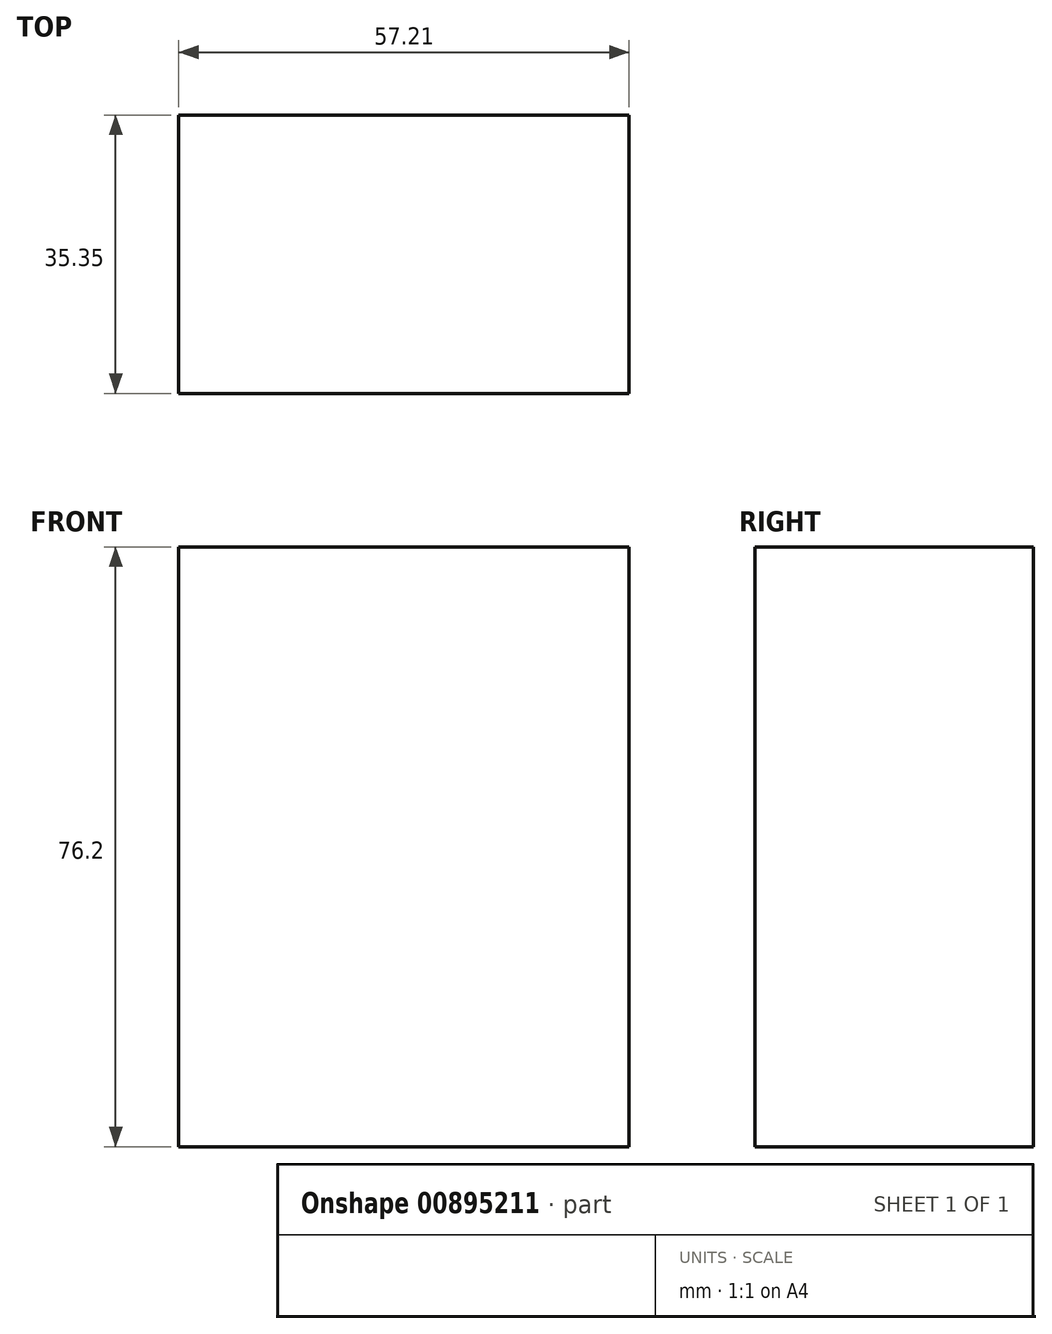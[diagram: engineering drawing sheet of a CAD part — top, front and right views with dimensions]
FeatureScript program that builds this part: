
annotation { "Feature Type Name" : "Feature", "Feature Type Description" : "" }
export const myFeature = defineFeature(function(context is Context, id is Id, definition is map)
    precondition{}
    {
        {
            var Q0;
            Q0=qCreatedBy(makeId("Top.planeOp"),FACE);
            var sketch = newSketch(context, id + "F0", { "sketchPlane" : qUnion([Q0])});
            skLineSegment(sketch, "E0.bottom", {"start": v(-24.07, 16.16) * mm, "end": v(33.14, 16.16) * mm});
            skLineSegment(sketch, "E0.top", {"start": v(-24.07, -19.19) * mm, "end": v(33.14, -19.19) * mm});
            skLineSegment(sketch, "E0.left", {"start": v(-24.07, 16.16) * mm, "end": v(-24.07, -19.19) * mm});
            skLineSegment(sketch, "E0.right", {"start": v(33.14, 16.16) * mm, "end": v(33.14, -19.19) * mm});
            skSolve(sketch);
        }
        {
            var Q0;
            Q0 = qSketchRegion(id + "F0", true);
            extrude(context, id + "F1", {"entities" : qUnion([Q0]), "depth" : 76.2 * mm, "offsetDistance" : 25.4 * mm});
        }
    });
